# Revit family: MAD-451-I_Pulsador analógico con aislador
name_source: partatom
category: Dispositivos de alarma de incendios
revit_build: Autodesk Revit 2017 (Build: 20190508_0315(x64)
units: mm (PartAtom-declared; Revit-internal decimal feet)

## family parameters
Anfitrión = Cara
Compartido = No
Corte con vacíos al cargar = No
Cota de conector redondo = Diámetro de uso
Mantener orientación de anotación = No
Punto de cálculo de habitación = No
Tipo de pieza = Normal

## types (1)
- MAD-451-I
    Altura = 98 mm
    Anchura = 98 mm
    Carga eléctrica = Otro
    Certificación = EN 54-11 y EN 54-17
    Comentarios de tipo = Los pulsadores analógicos son el medio por el cual se indican las alarmas de forma manual al sistema analógico de detección de incendio. Son un elemento imprescindible en cualquier instalación junto con los detectores puntuales.
    Conexionado = 2 x 1.5 mm² trenzado y apantallado
    Consumo en alarma = 3 mA
    Consumo en reposo = < 300 μA
    Código de montaje = PDETMAD-450-I
    Descripción = Pulsador de alarma analógico rearmable con aislador incorporado para montaje en superficie. Marca Detnov, modelo MAD-451-I. Incorpora led indicador de estado y llave de prueba. Color rojo. Certificados CPR EN 54-11 y EN 54-17. Dimensiones: 85 x 85 x 55 mm.
    Elevación por defecto = 1219 mm
    Fabricante = Detnov Security
    Fases = 1
    Humedad relativa = 95% sin condensación
    Imagen de tipo = <Ninguno>
    Modelo = Pulsador MAD-451-I
    Potencia total = 0 VA
    Profundidad = 48 mm
    Teléfono = (+34) 93 371 60 25
    Temperatura trabajo = De -5ºC a 55ºC
    Tensión de trabajo = De 22 a 38VDC
    URL = https://www.detnov.com
    Voltaje = 230 V
    Índice IP = IP40
